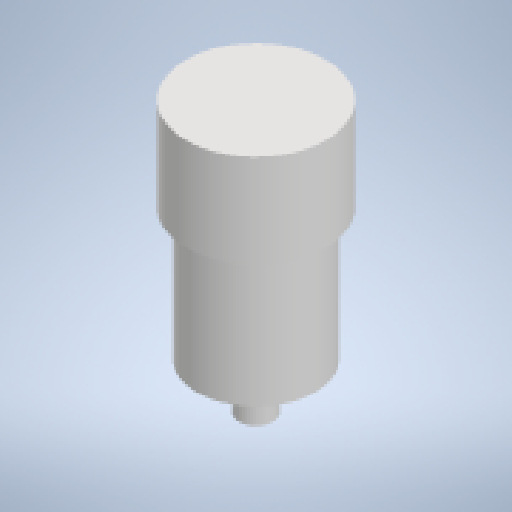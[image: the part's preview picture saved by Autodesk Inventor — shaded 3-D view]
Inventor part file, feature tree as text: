
AUTODESK INVENTOR PART (.ipt)
format: ipt  version: 2023 (Build 270158000, 158)  size: 148,480 bytes
history: native  units: in
note: dims shown in document units (in); Inventor stores cm internally (conversion verified against a paired STEP export)
features: revolve x1, sketch x1
ambient origin geometry x8: Origin, YZ Plane, XZ Plane, XY Plane, X Axis, Y Axis, Z Axis, Center Point
bodies: Solid1 (feature_tree)
feature tree (2):
  revolve  "Revolution1"  [1 undecoded]
  sketch  "Sketch1"  dims[d0=1.75in d1=3.8583in d2=360.0deg d3=0.1875in d4=1.378in d5=0.5in d6=2.0669in d7=2.7559in]
note: 1 required parameter value undecoded (feature->parameter linkage not recoverable at this tier; creation-order binding heuristic only, values carry confidence <= 0.55)
